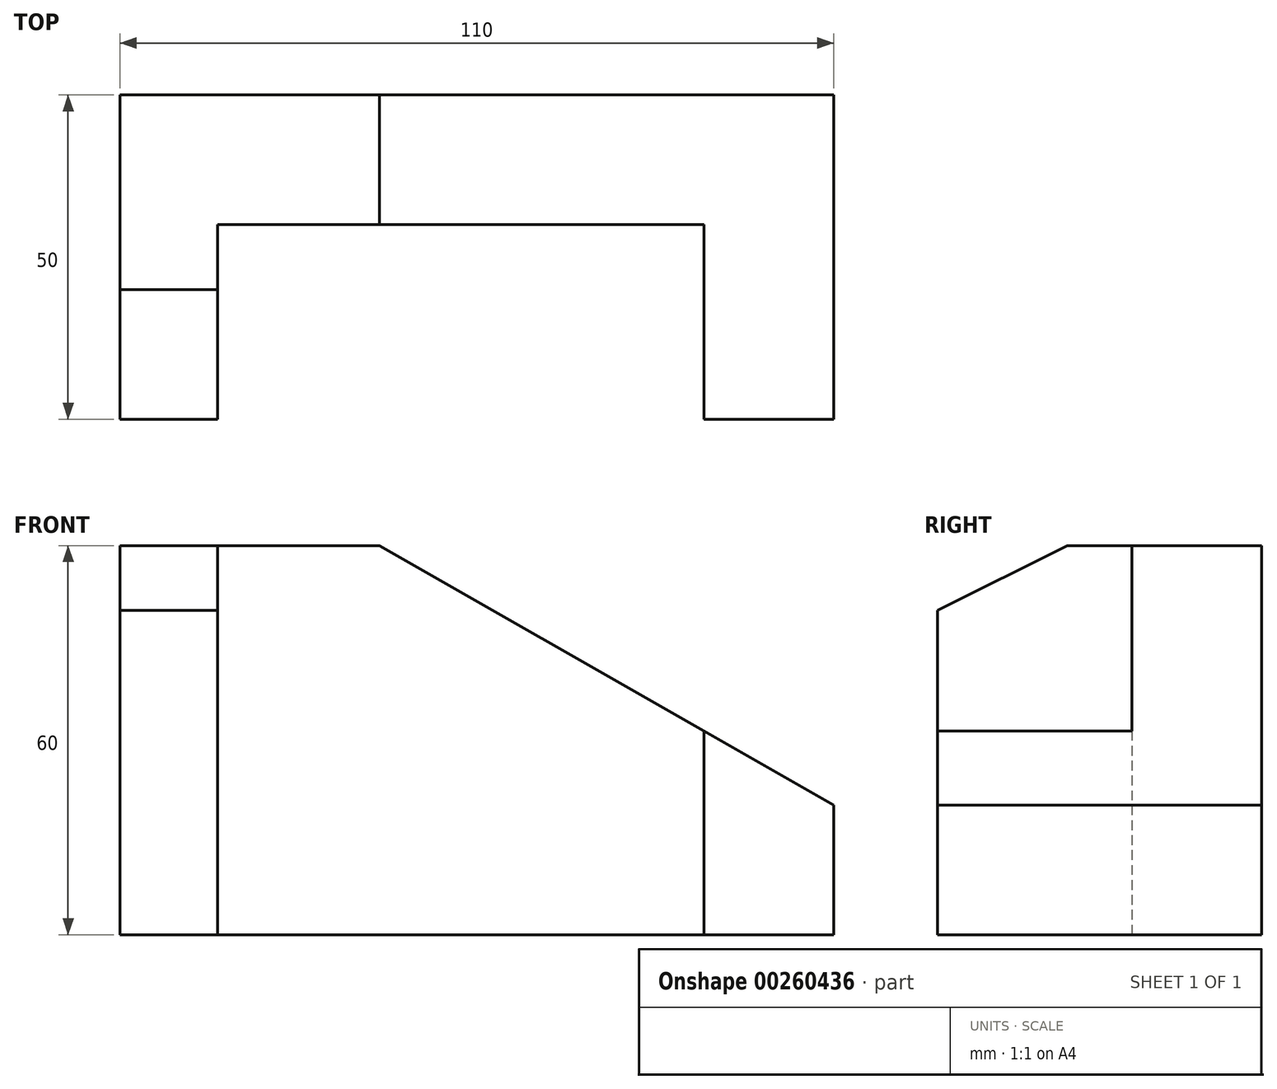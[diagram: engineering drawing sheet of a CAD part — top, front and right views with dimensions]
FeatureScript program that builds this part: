
annotation { "Feature Type Name" : "Feature", "Feature Type Description" : "" }
export const myFeature = defineFeature(function(context is Context, id is Id, definition is map)
    precondition{}
    {
        {
            assignVariable(context, id + "F0", {"name" : "C", "anyValue" : 50});
        }
        {
            var Q0;
            Q0=qCreatedBy(makeId("Front.planeOp"),FACE);
            var sketch = newSketch(context, id + "F1", { "sketchPlane" : qUnion([Q0])});
            skLineSegment(sketch, "E0", {"start": v(0, 0) * mm, "end": v(0, 60) * mm});
            skLineSegment(sketch, "E1", {"start": v(0, 60) * mm, "end": v(40, 60) * mm});
            skLineSegment(sketch, "E2", {"start": v(40, 60) * mm, "end": v(110, 20) * mm});
            skLineSegment(sketch, "E3", {"start": v(110, 20) * mm, "end": v(110, 0) * mm});
            skLineSegment(sketch, "E4", {"start": v(110, 0) * mm, "end": v(0, 0) * mm});
            skSolve(sketch);
        }
        {
            var Q0;
            Q0 = qSketchRegion(id + "F1", true);
            extrude(context, id + "F2", {"entities" : qUnion([Q0]), "depth" : (getVariable(context, 'C')) * mm});
        }
        {
            var Q0;
            Q0=makeQuery(id+"F2.opExtrude","SWEPT_FACE",FACE,{"disambiguationData":[OSD([sQuery(id+"F1.wireOp",EDGE,"E4")])]});
            var sketch = newSketch(context, id + "F3", { "sketchPlane" : qUnion([Q0])});
            skLineSegment(sketch, "E5.bottom", {"start": v(15, 50) * mm, "end": v(90, 50) * mm});
            skLineSegment(sketch, "E5.top", {"start": v(15, 20) * mm, "end": v(90, 20) * mm});
            skLineSegment(sketch, "E5.left", {"start": v(15, 50) * mm, "end": v(15, 20) * mm});
            skLineSegment(sketch, "E5.right", {"start": v(90, 50) * mm, "end": v(90, 20) * mm});
            skSolve(sketch);
        }
        {
            var Q0;
            Q0 = qSketchRegion(id + "F3", true);
            extrude(context, id + "F4", {"entities" : qUnion([Q0]), "operationType" : NewBodyOperationType.REMOVE, "oppositeDirection" : true, "depth" : 98 * mm});
        }
        {
            var Q0;
            Q0=makeQuery(id+"F2.opExtrude","SWEPT_FACE",FACE,{"disambiguationData":[OSD([sQuery(id+"F1.wireOp",EDGE,"E0")])]});
            var sketch = newSketch(context, id + "F5", { "sketchPlane" : qUnion([Q0])});
            skLineSegment(sketch, "E6", {"start": v(30, 60) * mm, "end": v(50, 50) * mm});
            skSolve(sketch);
        }
        {
            var Q0;
            Q0 = qSketchRegion(id + "F5", true);
            var Q1;
            {var subQ0=sQuery(id+"F5.wireOp",EDGE,"E6");Q1=makeQuery(id+"F5.imprint","IMPRINT",FACE,{"disambiguationData":[TD([[makeQuery(id+"F5.imprint","IMPRINT",EDGE,{"derivedFrom":subQ0}),1.0]])]});}
            extrude(context, id + "F6", {"entities" : qUnion([Q0, Q1]), "operationType" : NewBodyOperationType.REMOVE, "oppositeDirection" : true, "depth" : 105.3 * mm});
        }
    });
